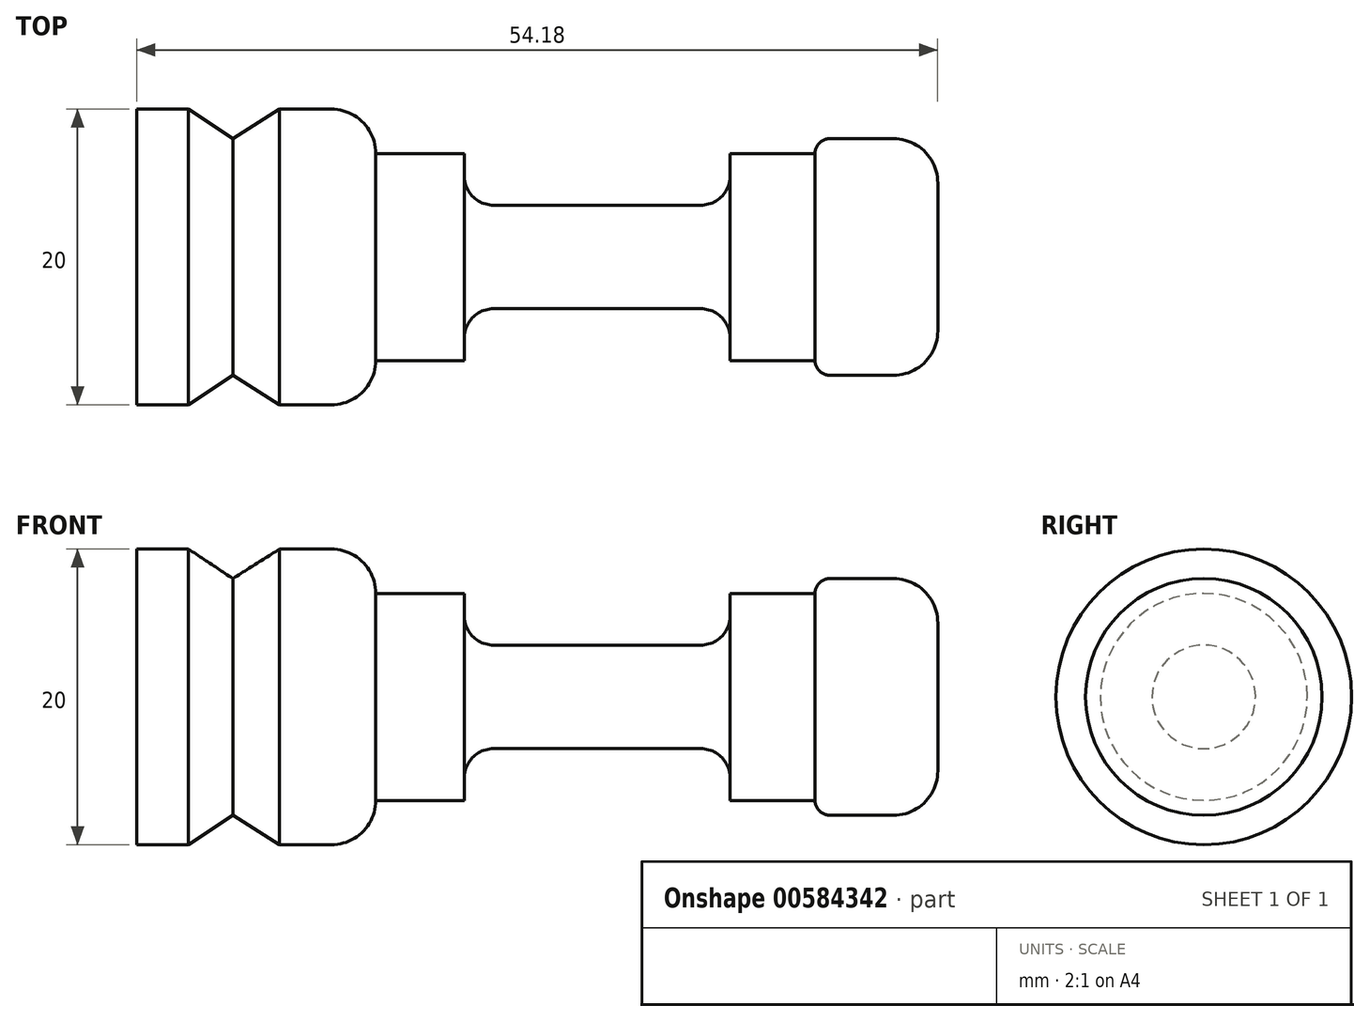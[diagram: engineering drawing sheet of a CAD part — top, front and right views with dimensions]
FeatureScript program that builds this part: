
annotation { "Feature Type Name" : "Feature", "Feature Type Description" : "" }
export const myFeature = defineFeature(function(context is Context, id is Id, definition is map)
    precondition{}
    {
        {
            var Q0;
            Q0=qCreatedBy(makeId("Front.planeOp"),FACE);
            var sketch = newSketch(context, id + "F0", { "sketchPlane" : qUnion([Q0])});
            skLineSegment(sketch, "E0", {"start": v(0, 0) * mm, "end": v(-28.8, 0) * mm});
            skLineSegment(sketch, "E1", {"start": v(-28.8, 0) * mm, "end": v(26.2, 0) * mm});
            skLineSegment(sketch, "E2", {"start": v(-28.8, 0) * mm, "end": v(-28.8, -10) * mm});
            skLineSegment(sketch, "E3", {"start": v(-28.8, -10) * mm, "end": v(-25.3, -10) * mm});
            skLineSegment(sketch, "E4", {"start": v(-25.3, -10) * mm, "end": v(-22.3, -8) * mm});
            skLineSegment(sketch, "E5", {"start": v(-22.3, 0) * mm, "end": v(-22.3, -8) * mm});
            skLineSegment(sketch, "E6", {"start": v(-19.12, 0) * mm, "end": v(-19.12, -10) * mm});
            skLineSegment(sketch, "E7", {"start": v(-22.3, -8) * mm, "end": v(-19.12, -10) * mm});
            skLineSegment(sketch, "E8", {"start": v(-25.3, -10) * mm, "end": v(-25.3, 0) * mm});
            skPoint(sketch, "E9.startSnap0", {"position": v(-22.3, -4) * mm});
            skLineSegment(sketch, "E10", {"start": v(-19.12, -10) * mm, "end": v(-15.62, -10) * mm});
            skPoint(sketch, "E11.visualSharp", {"position": v(-12.62, -10) * mm});
            skArc(sketch, "E11.filletArc", {"start": v(-15.62, -10) * mm, "mid": v(-13.5, -9.12) * mm, "end": v(-12.62, -7) * mm});
            skLineSegment(sketch, "E12", {"start": v(-12.64, -7) * mm, "end": v(-6.64, -7) * mm});
            skLineSegment(sketch, "E13", {"start": v(-6.64, -7) * mm, "end": v(-6.64, -5.5) * mm});
            skLineSegment(sketch, "E14", {"start": v(11.36, -5.5) * mm, "end": v(11.36, -7) * mm});
            skLineSegment(sketch, "E15", {"start": v(-4.64, -3.5) * mm, "end": v(9.36, -3.5) * mm});
            skLineSegment(sketch, "E16", {"start": v(11.36, -7) * mm, "end": v(17.09, -7) * mm});
            skLineSegment(sketch, "E17", {"start": v(17.09, -7) * mm, "end": v(17.09, -7) * mm});
            skLineSegment(sketch, "E18", {"start": v(18.09, -8) * mm, "end": v(22.4, -8) * mm});
            skLineSegment(sketch, "E19", {"start": v(25.4, -5) * mm, "end": v(25.4, 0) * mm});
            skPoint(sketch, "E20.visualSharp", {"position": v(25.4, -8) * mm});
            skArc(sketch, "E20.filletArc", {"start": v(22.4, -8) * mm, "mid": v(24.52, -7.12) * mm, "end": v(25.4, -5) * mm});
            skPoint(sketch, "E21.visualSharp", {"position": v(17.09, -8) * mm});
            skArc(sketch, "E21.filletArc", {"start": v(17.09, -7) * mm, "mid": v(17.38, -7.7) * mm, "end": v(18.09, -8) * mm});
            skPoint(sketch, "E22.newPointA", {"position": v(-6.64, 0) * mm});
            skPoint(sketch, "E22.newPointB", {"position": v(-6.64, -3.5) * mm});
            skArc(sketch, "E22.filletArc", {"start": v(-4.64, -3.5) * mm, "mid": v(-6.06, -4.09) * mm, "end": v(-6.64, -5.5) * mm});
            skPoint(sketch, "E23.start.orphan", {"position": v(-12.62, 0) * mm});
            skPoint(sketch, "E24.orphan", {"position": v(11.36, 0) * mm});
            skPoint(sketch, "E25.visualSharp", {"position": v(11.36, -3.5) * mm});
            skArc(sketch, "E25.filletArc", {"start": v(11.36, -5.5) * mm, "mid": v(10.77, -4.09) * mm, "end": v(9.36, -3.5) * mm});
            skLineSegment(sketch, "E26", {"start": v(-42.92, 0) * mm, "end": v(30.99, 0) * mm, "construction": true});
            skSolve(sketch);
        }
        {
            var Q0;
            {var subQ0=sQuery(id+"F0.wireOp",EDGE,"E2");Q0=makeQuery(id+"F0.imprint","IMPRINT",FACE,{"disambiguationData":[TD([[makeQuery(id+"F0.imprint","IMPRINT",EDGE,{"derivedFrom":subQ0}),1.0]])]});}
            var Q1;
            {var subQ3=sQuery(id+"F0.wireOp",EDGE,"E6");Q1=makeQuery(id+"F0.imprint","IMPRINT",FACE,{"disambiguationData":[TD([[makeQuery(id+"F0.imprint","IMPRINT",EDGE,{"derivedFrom":subQ3}),1.0]])]});}
            var Q2;
            Q2=makeQuery(id+"F0.imprint","IMPRINT",FACE,{"disambiguationData":[TD([[makeQuery(id+"F0.imprint","IMPRINT",EDGE,{"derivedFrom":sQuery(id+"F0.wireOp",EDGE,"E4")}),1.0]])]});
            var Q3;
            {var subQ0=sQuery(id+"F0.wireOp",EDGE,"E5");Q3=makeQuery(id+"F0.imprint","IMPRINT",FACE,{"disambiguationData":[TD([[makeQuery(id+"F0.imprint","IMPRINT",EDGE,{"derivedFrom":subQ0}),1.0]])]});}
            var Q4;
            Q4=sQuery(id+"F0.wireOp",EDGE,"E26");
            revolve(context, id + "F1", {"entities" : qUnion([Q0, Q1, Q2, Q3]), "axis" : qUnion([Q4]), "revolveType" : RevolveType.FULL});
        }
    });
